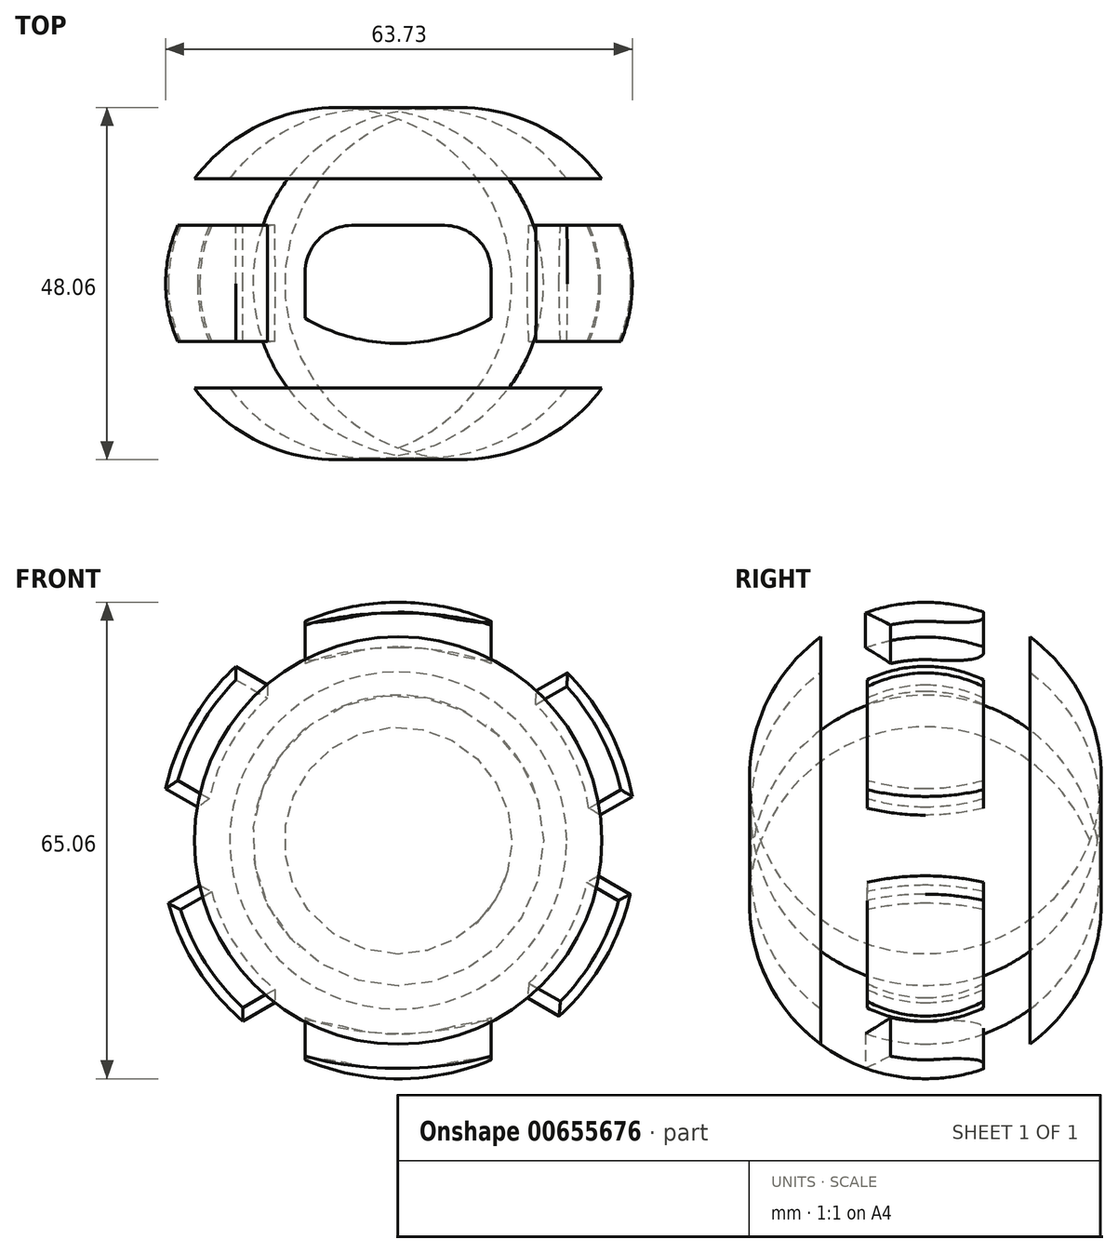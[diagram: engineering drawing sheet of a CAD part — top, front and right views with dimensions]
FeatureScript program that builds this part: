
annotation { "Feature Type Name" : "Feature", "Feature Type Description" : "" }
export const myFeature = defineFeature(function(context is Context, id is Id, definition is map)
    precondition{}
    {
        {
            var Q0;
            Q0=qCreatedBy(makeId("Top.planeOp"),FACE);
            var sketch = newSketch(context, id + "F0", { "sketchPlane" : qUnion([Q0])});
            skLineSegment(sketch, "E0", {"start": v(0, 0) * mm, "end": v(23.02, 0) * mm});
            skLineSegment(sketch, "E1", {"start": v(23.02, 0) * mm, "end": v(23.02, -28.58) * mm});
            skLineSegment(sketch, "E2", {"start": v(23.02, -28.58) * mm, "end": v(0, -28.58) * mm});
            skLineSegment(sketch, "E3.MirrorCS", {"start": v(0, 0) * mm, "end": v(-23.02, 0) * mm});
            skLineSegment(sketch, "E4.MirrorCS", {"start": v(-23.02, -28.58) * mm, "end": v(0, -28.58) * mm});
            skLineSegment(sketch, "E5.MirrorCS", {"start": v(-23.02, 0) * mm, "end": v(-23.02, -28.58) * mm});
            skLineSegment(sketch, "E6", {"start": v(23.02, -14.29) * mm, "end": v(-27.78, -14.29) * mm});
            skArc(sketch, "E7", {"start": v(-23.02, 0) * mm, "mid": v(-27.78, -14.29) * mm, "end": v(-23.02, -28.58) * mm});
            skLineSegment(sketch, "E8", {"start": v(0, 0) * mm, "end": v(0, -28.58) * mm});
            skLineSegment(sketch, "E9", {"start": v(-23.02, -28.58) * mm, "end": v(-27.82, -28.58) * mm});
            skLineSegment(sketch, "E10", {"start": v(-23.02, 0) * mm, "end": v(-27.82, 0) * mm});
            skLineSegment(sketch, "E11", {"start": v(-27.78, -14.29) * mm, "end": v(-23.02, -14.29) * mm});
            skLineSegment(sketch, "E12", {"start": v(-27.78, -14.29) * mm, "end": v(-32.53, -14.29) * mm});
            skArc(sketch, "E13", {"start": v(-27.82, 0) * mm, "mid": v(-32.53, -14.29) * mm, "end": v(-27.82, -28.58) * mm});
            skSolve(sketch);
        }
        {
            var Q0;
            {var subQ0=sQuery(id+"F0.wireOp",EDGE,"E9");Q0=makeQuery(id+"F0.imprint","IMPRINT",FACE,{"disambiguationData":[TD([[makeQuery(id+"F0.imprint","IMPRINT",EDGE,{"derivedFrom":subQ0}),-1.0]])]});}
            var Q1;
            {var subQ0=sQuery(id+"F0.wireOp",EDGE,"E10");Q1=makeQuery(id+"F0.imprint","IMPRINT",FACE,{"disambiguationData":[TD([[makeQuery(id+"F0.imprint","IMPRINT",EDGE,{"derivedFrom":subQ0}),1.0]])]});}
            var Q2;
            Q2=sQuery(id+"F0.wireOp",EDGE,"E8");
            revolve(context, id + "F1", {"entities" : qUnion([Q0, Q1]), "axis" : qUnion([Q2]), "revolveType" : RevolveType.FULL});
        }
        {
            var Q0;
            Q0=qCreatedBy(makeId("Top.planeOp"),FACE);
            cPlane(context, id + "F2", {"entities" : qUnion([Q0]), "cplaneType" : CPlaneType.OFFSET, "offset" : 25.4 * mm, "width" : 152.4 * mm, "height" : 152.4 * mm});
        }
        {
            var Q0;
            Q0=qCreatedBy(id+"F2.planeOp",FACE);
            cPlane(context, id + "F3", {"entities" : qUnion([Q0]), "cplaneType" : CPlaneType.OFFSET, "offset" : 50.8 * mm, "width" : 152.4 * mm, "height" : 152.4 * mm});
        }
        {
            var Q0;
            Q0=qCreatedBy(makeId("Top.planeOp"),FACE);
            var Q1;
            Q1=makeQuery(id+"F1.opRevolve","SWEPT_EDGE",EDGE,{"disambiguationData":[OSD([sQuery(id+"F0.wireOp",EDGE,"E3.MirrorCS"),sQuery(id+"F0.wireOp",EDGE,"E5.MirrorCS"),sQuery(id+"F0.wireOp",EDGE,"E7"),sQuery(id+"F0.wireOp",EDGE,"E10")])]});
            cPlane(context, id + "F4", {"entities" : qUnion([Q0, Q1]), "cplaneType" : CPlaneType.LINE_ANGLE, "offset" : 25.4 * mm, "angle" : 60 * degree, "width" : 152.4 * mm, "height" : 152.4 * mm});
        }
        {
            var Q0;
            Q0=qCreatedBy(id+"F4.planeOp",FACE);
            cPlane(context, id + "F5", {"entities" : qUnion([Q0]), "cplaneType" : CPlaneType.OFFSET, "offset" : 50.8 * mm, "oppositeDirection" : true, "width" : 152.4 * mm, "height" : 152.4 * mm});
        }
        {
            var Q0;
            Q0=qCreatedBy(id+"F4.planeOp",FACE);
            var Q1;
            Q1=makeQuery(id+"F1.opRevolve","SWEPT_EDGE",EDGE,{"disambiguationData":[OSD([sQuery(id+"F0.wireOp",EDGE,"E3.MirrorCS"),sQuery(id+"F0.wireOp",EDGE,"E5.MirrorCS"),sQuery(id+"F0.wireOp",EDGE,"E7"),sQuery(id+"F0.wireOp",EDGE,"E10")])]});
            cPlane(context, id + "F6", {"entities" : qUnion([Q0, Q1]), "cplaneType" : CPlaneType.LINE_ANGLE, "offset" : 25.4 * mm, "angle" : 60 * degree, "width" : 152.4 * mm, "height" : 152.4 * mm});
        }
        {
            var Q0;
            Q0=qCreatedBy(id+"F6.planeOp",FACE);
            cPlane(context, id + "F7", {"entities" : qUnion([Q0]), "cplaneType" : CPlaneType.OFFSET, "offset" : 50.8 * mm, "width" : 152.4 * mm, "height" : 152.4 * mm});
        }
        {
            var Q0;
            Q0=qCreatedBy(id+"F3.planeOp",FACE);
            cPlane(context, id + "F8", {"entities" : qUnion([Q0]), "cplaneType" : CPlaneType.OFFSET, "offset" : 152.4 * mm, "oppositeDirection" : true, "width" : 152.4 * mm, "height" : 152.4 * mm});
        }
        {
            var Q0;
            Q0=qCreatedBy(id+"F5.planeOp",FACE);
            var sketch = newSketch(context, id + "F9", { "sketchPlane" : qUnion([Q0])});
            skLineSegment(sketch, "E14", {"start": v(0, -1.25) * mm, "end": v(6.35, -1.25) * mm});
            skLineSegment(sketch, "E15", {"start": v(6.35, -1.25) * mm, "end": v(6.35, -9.2) * mm});
            skLineSegment(sketch, "E16", {"start": v(6.35, -9.2) * mm, "end": v(22.23, -9.2) * mm});
            skLineSegment(sketch, "E17", {"start": v(22.23, -9.2) * mm, "end": v(22.23, -1.25) * mm});
            skLineSegment(sketch, "E18.MirrorCS", {"start": v(6.35, -1.25) * mm, "end": v(6.35, 6.68) * mm});
            skLineSegment(sketch, "E19.MirrorCS", {"start": v(6.35, 6.68) * mm, "end": v(22.23, 6.68) * mm});
            skLineSegment(sketch, "E20.MirrorCS", {"start": v(22.23, 6.68) * mm, "end": v(22.23, -1.25) * mm});
            skArc(sketch, "E21", {"start": v(22.23, 6.68) * mm, "mid": v(14.29, 8.27) * mm, "end": v(6.35, 6.68) * mm});
            skArc(sketch, "E22", {"start": v(6.35, -9.2) * mm, "mid": v(14.29, -10.77) * mm, "end": v(22.23, -9.2) * mm});
            skSolve(sketch);
        }
        {
            var Q0;
            Q0=makeQuery(id+"F9.imprint","IMPRINT",FACE,{"disambiguationData":[TD([[makeQuery(id+"F9.imprint","IMPRINT",EDGE,{"derivedFrom":sQuery(id+"F9.wireOp",EDGE,"E15")}),1.0]])]});
            var Q1;
            Q1=makeQuery(id+"F9.imprint","IMPRINT",FACE,{"disambiguationData":[TD([[makeQuery(id+"F9.imprint","IMPRINT",EDGE,{"derivedFrom":sQuery(id+"F9.wireOp",EDGE,"E16")}),-1.0]])]});
            var Q2;
            Q2=makeQuery(id+"F9.imprint","IMPRINT",FACE,{"disambiguationData":[TD([[makeQuery(id+"F9.imprint","IMPRINT",EDGE,{"derivedFrom":sQuery(id+"F9.wireOp",EDGE,"E19.MirrorCS")}),1.0]])]});
            extrude(context, id + "F10", {"entities" : qUnion([Q0, Q1, Q2]), "operationType" : NewBodyOperationType.REMOVE, "depth" : 228.6 * mm, "offsetDistance" : 25.4 * mm});
        }
        {
            var Q0;
            Q0=qCreatedBy(id+"F7.planeOp",FACE);
            var sketch = newSketch(context, id + "F11", { "sketchPlane" : qUnion([Q0])});
            skLineSegment(sketch, "E23", {"start": v(0, 0) * mm, "end": v(-6.35, 0) * mm});
            skLineSegment(sketch, "E24", {"start": v(-6.35, 0) * mm, "end": v(-6.35, -7.94) * mm});
            skLineSegment(sketch, "E25", {"start": v(-6.35, -7.94) * mm, "end": v(-22.23, -7.94) * mm});
            skLineSegment(sketch, "E26", {"start": v(-22.23, -7.94) * mm, "end": v(-22.23, 0) * mm});
            skLineSegment(sketch, "E27.MirrorCS", {"start": v(-6.35, 0) * mm, "end": v(-6.35, 7.94) * mm});
            skLineSegment(sketch, "E28.MirrorCS", {"start": v(-6.35, 7.94) * mm, "end": v(-22.23, 7.94) * mm});
            skLineSegment(sketch, "E29.MirrorCS", {"start": v(-22.23, 7.94) * mm, "end": v(-22.23, 0) * mm});
            skArc(sketch, "E30", {"start": v(-6.35, 7.94) * mm, "mid": v(-14.29, 9.5) * mm, "end": v(-22.23, 7.94) * mm});
            skArc(sketch, "E31", {"start": v(-22.23, -7.94) * mm, "mid": v(-14.29, -9.77) * mm, "end": v(-6.35, -7.94) * mm});
            skSolve(sketch);
        }
        {
            var Q0;
            Q0=makeQuery(id+"F11.imprint","IMPRINT",FACE,{"disambiguationData":[TD([[makeQuery(id+"F11.imprint","IMPRINT",EDGE,{"derivedFrom":sQuery(id+"F11.wireOp",EDGE,"E24")}),-1.0]])]});
            extrude(context, id + "F12", {"entities" : qUnion([Q0]), "operationType" : NewBodyOperationType.REMOVE, "oppositeDirection" : true, "depth" : 228.6 * mm, "offsetDistance" : 25.4 * mm});
        }
        {
            var Q0;
            Q0=qCreatedBy(id+"F8.planeOp",FACE);
            var sketch = newSketch(context, id + "F13", { "sketchPlane" : qUnion([Q0])});
            skLineSegment(sketch, "E32", {"start": v(0, 0) * mm, "end": v(0, -6.35) * mm});
            skLineSegment(sketch, "E33", {"start": v(0, -6.35) * mm, "end": v(12.7, -6.35) * mm});
            skLineSegment(sketch, "E34", {"start": v(12.7, -6.35) * mm, "end": v(12.7, -19.05) * mm});
            skLineSegment(sketch, "E35", {"start": v(12.7, -19.05) * mm, "end": v(-12.7, -19.05) * mm});
            skLineSegment(sketch, "E36", {"start": v(-12.7, -19.05) * mm, "end": v(-12.7, -6.35) * mm});
            skLineSegment(sketch, "E37", {"start": v(-12.7, -6.35) * mm, "end": v(0, -6.35) * mm});
            skArc(sketch, "E38", {"start": v(-12.7, -19.05) * mm, "mid": v(0, -22.45) * mm, "end": v(12.7, -19.05) * mm});
            skSolve(sketch);
        }
        {
            var Q0;
            Q0=makeQuery(id+"F13.imprint","IMPRINT",FACE,{"disambiguationData":[TD([[makeQuery(id+"F13.imprint","IMPRINT",EDGE,{"derivedFrom":sQuery(id+"F13.wireOp",EDGE,"E33")}),-1.0]])]});
            extrude(context, id + "F14", {"entities" : qUnion([Q0]), "operationType" : NewBodyOperationType.REMOVE, "depth" : 228.6 * mm, "offsetDistance" : 25.4 * mm});
        }
        {
            var Q0;
            Q0 = qSketchRegion(id + "F13", true);
            extrude(context, id + "F15", {"entities" : qUnion([Q0]), "operationType" : NewBodyOperationType.REMOVE, "depth" : 228.6 * mm, "offsetDistance" : 25.4 * mm});
        }
        {
            var Q0;
            Q0=makeQuery(id+"F14.boolean.opBoolean","COPY",EDGE,{"disambiguationData":[OD(0.0)],"derivedFrom":makeQuery(id+"F14.opExtrude","SWEPT_EDGE",EDGE,{"disambiguationData":[OSD([sQuery(id+"F13.wireOp",EDGE,"E36"),sQuery(id+"F13.wireOp",EDGE,"E37")])]})});
            var Q1;
            Q1=makeQuery(id+"F14.boolean.opBoolean","COPY",EDGE,{"disambiguationData":[OD(0.0)],"derivedFrom":makeQuery(id+"F14.opExtrude","SWEPT_EDGE",EDGE,{"disambiguationData":[OSD([sQuery(id+"F13.wireOp",EDGE,"E33"),sQuery(id+"F13.wireOp",EDGE,"E34")])]})});
            var Q2;
            Q2=makeQuery(id+"F14.boolean.opBoolean","COPY",EDGE,{"disambiguationData":[OD(1.0)],"derivedFrom":makeQuery(id+"F14.opExtrude","SWEPT_EDGE",EDGE,{"disambiguationData":[OSD([sQuery(id+"F13.wireOp",EDGE,"E33"),sQuery(id+"F13.wireOp",EDGE,"E34")])]})});
            var Q3;
            Q3=makeQuery(id+"F14.boolean.opBoolean","COPY",EDGE,{"disambiguationData":[OD(1.0)],"derivedFrom":makeQuery(id+"F14.opExtrude","SWEPT_EDGE",EDGE,{"disambiguationData":[OSD([sQuery(id+"F13.wireOp",EDGE,"E36"),sQuery(id+"F13.wireOp",EDGE,"E37")])]})});
            fillet(context, id + "F16", {"entities" : qUnion([Q0, Q1, Q2, Q3]), "radius" : 6.35 * mm, "tangentPropagation" : true, "allowEdgeOverflow" : false});
        }
        {
            var Q0;
            Q0 = qSketchRegion(id + "F11", true);
            extrude(context, id + "F17", {"entities" : qUnion([Q0]), "operationType" : NewBodyOperationType.REMOVE, "oppositeDirection" : true, "depth" : 228.6 * mm, "offsetDistance" : 25.4 * mm});
        }
    });
